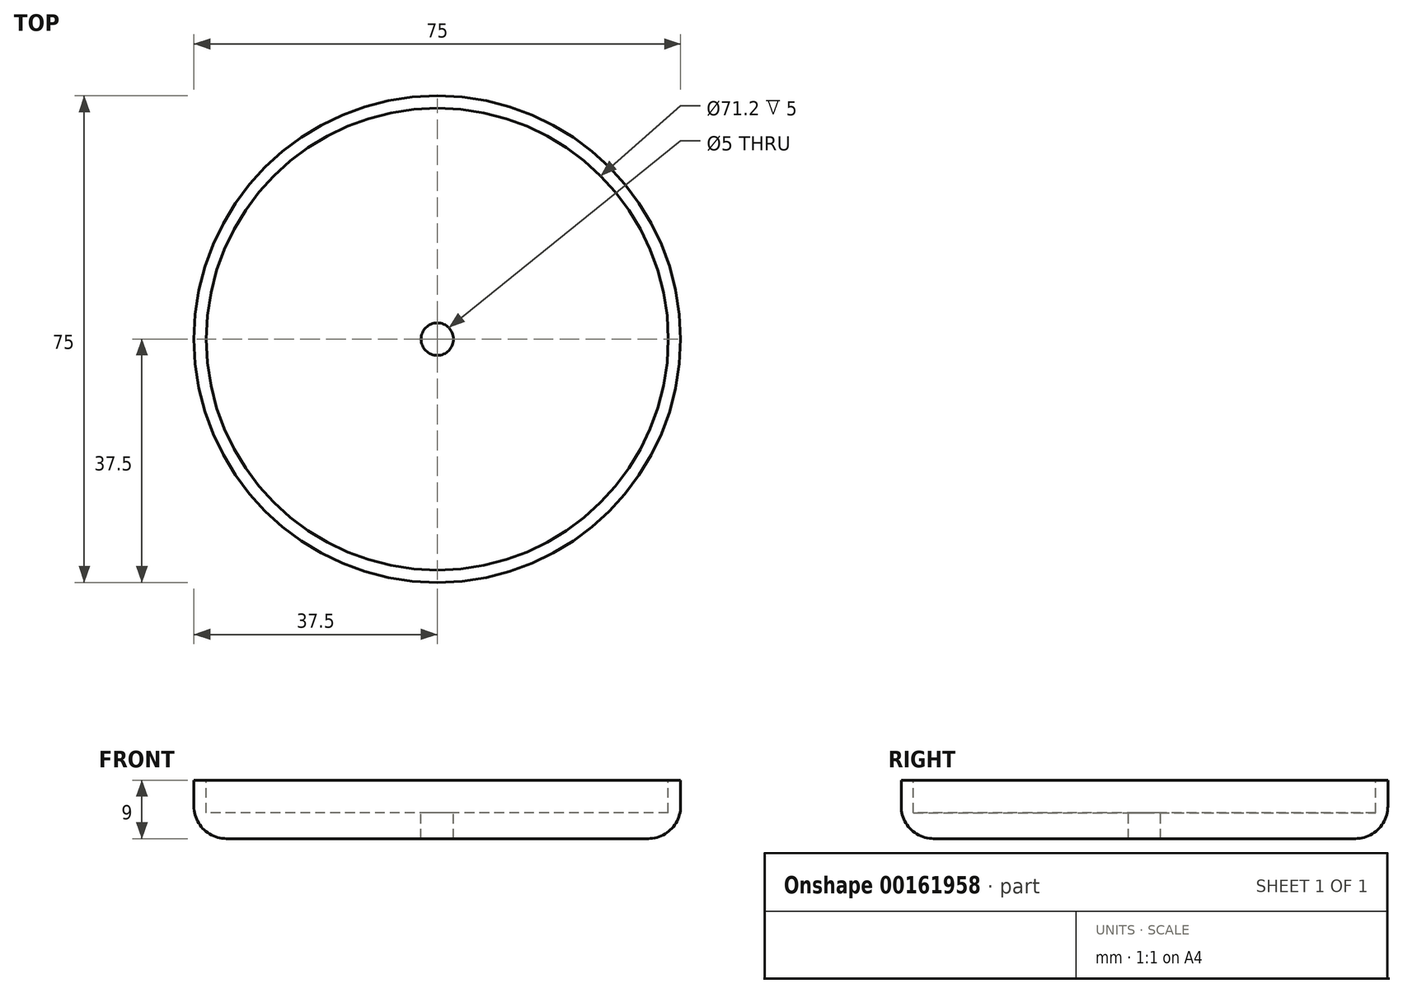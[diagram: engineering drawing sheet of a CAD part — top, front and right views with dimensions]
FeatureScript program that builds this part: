
annotation { "Feature Type Name" : "Feature", "Feature Type Description" : "" }
export const myFeature = defineFeature(function(context is Context, id is Id, definition is map)
    precondition{}
    {
        {
            var Q0;
            Q0=qCreatedBy(makeId("Top.planeOp"),FACE);
            var sketch = newSketch(context, id + "F0", { "sketchPlane" : qUnion([Q0])});
            skCircle(sketch, "E0", {"center": v(0, 0) * mm, "radius": 37.5 * mm});
            skSolve(sketch);
        }
        {
            var Q0;
            Q0 = qSketchRegion(id + "F0", true);
            extrude(context, id + "F1", {"entities" : qUnion([Q0]), "depth" : 4 * mm});
        }
        {
            var Q0;
            Q0=makeQuery(id+"F1.opExtrude","CAP_FACE",FACE,{"disambiguationData":[OSD([sQuery(id+"F0.wireOp",EDGE,"E0")])],"isStart":false});
            var sketch = newSketch(context, id + "F2", { "sketchPlane" : qUnion([Q0])});
            skCircle(sketch, "E1", {"center": v(0, 0) * mm, "radius": 33.5 * mm});
            skCircle(sketch, "E2", {"center": v(0, 0) * mm, "radius": 37.5 * mm});
            skSolve(sketch);
        }
        {
            var Q0;
            Q0 = qSketchRegion(id + "F2", true);
            extrude(context, id + "F3", {"entities" : qUnion([Q0]), "operationType" : NewBodyOperationType.ADD, "depth" : 5 * mm});
        }
        {
            var Q0;
            Q0=makeQuery(id+"F3.opExtrude","CAP_FACE",FACE,{"disambiguationData":[OSD([sQuery(id+"F2.wireOp",EDGE,"E1"),sQuery(id+"F2.wireOp",EDGE,"E2")])],"isStart":false});
            var sketch = newSketch(context, id + "F4", { "sketchPlane" : qUnion([Q0])});
            skCircle(sketch, "E3", {"center": v(0, 0) * mm, "radius": 35.6 * mm});
            skSolve(sketch);
        }
        {
            var Q0;
            Q0 = qSketchRegion(id + "F4", true);
            extrude(context, id + "F5", {"entities" : qUnion([Q0]), "operationType" : NewBodyOperationType.REMOVE, "oppositeDirection" : true, "depth" : 5 * mm});
        }
        {
            var Q0;
            Q0=makeQuery(id+"F5.boolean.opBoolean","MERGE",FACE,{"derivedFrom":[makeQuery(id+"F1.opExtrude","CAP_FACE",FACE,{"disambiguationData":[OSD([sQuery(id+"F0.wireOp",EDGE,"E0")])],"isStart":false}),makeQuery(id+"F5.opExtrude","CAP_FACE",FACE,{"disambiguationData":[OSD([sQuery(id+"F4.wireOp",EDGE,"E3")])],"isStart":false})]});
            var sketch = newSketch(context, id + "F6", { "sketchPlane" : qUnion([Q0])});
            skCircle(sketch, "E4", {"center": v(0, 0) * mm, "radius": 2.5 * mm});
            skSolve(sketch);
        }
        {
            var Q0;
            Q0 = qSketchRegion(id + "F6", true);
            extrude(context, id + "F7", {"entities" : qUnion([Q0]), "operationType" : NewBodyOperationType.REMOVE, "endBound" : BoundingType.THROUGH_ALL, "oppositeDirection" : true, "depth" : 25 * mm});
        }
        {
            var Q0;
            Q0=makeQuery(id+"F1.opExtrude","CAP_EDGE",EDGE,{"disambiguationData":[OSD([sQuery(id+"F0.wireOp",EDGE,"E0")])],"isStart":true});
            fillet(context, id + "F8", {"entities" : qUnion([Q0]), "radius" : 5 * mm, "tangentPropagation" : true, "allowEdgeOverflow" : false});
        }
    });
